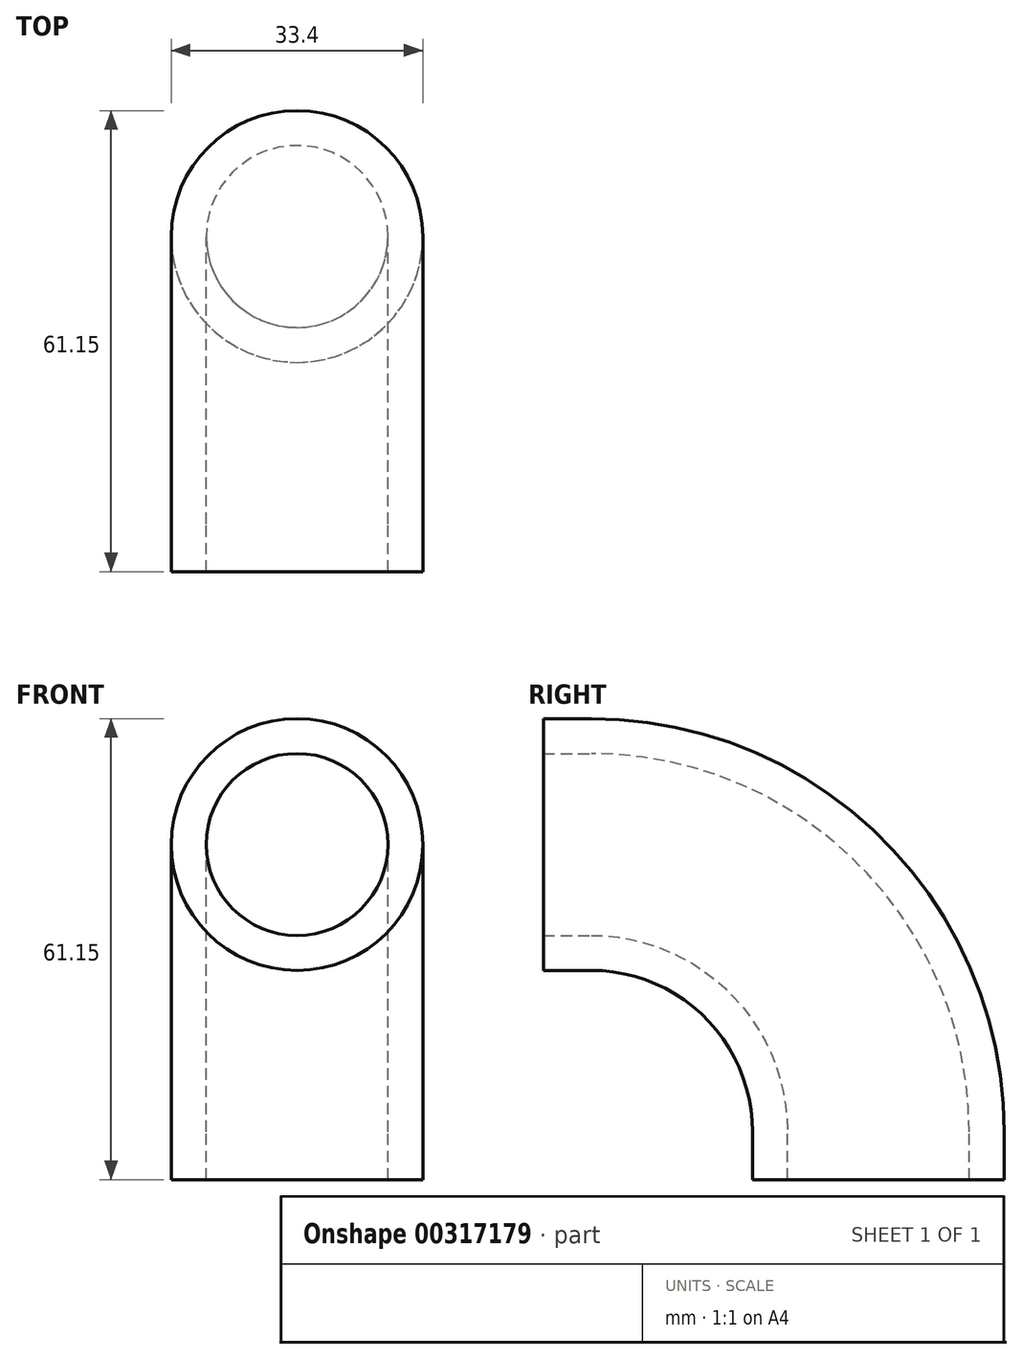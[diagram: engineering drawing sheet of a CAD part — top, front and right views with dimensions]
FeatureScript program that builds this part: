
annotation { "Feature Type Name" : "Feature", "Feature Type Description" : "" }
export const myFeature = defineFeature(function(context is Context, id is Id, definition is map)
    precondition{}
    {
        {
            var Q0;
            Q0=qCreatedBy(makeId("Right.planeOp"),FACE);
            var sketch = newSketch(context, id + "F0", { "sketchPlane" : qUnion([Q0])});
            skArc(sketch, "E0", {"start": v(38.1, 0) * mm, "mid": v(26.94, 26.94) * mm, "end": v(0, 38.1) * mm});
            skSolve(sketch);
        }
        {
            var Q0;
            Q0=qCreatedBy(makeId("Front.planeOp"),FACE);
            var sketch = newSketch(context, id + "F1", { "sketchPlane" : qUnion([Q0])});
            skCircle(sketch, "E1", {"center": v(0, 38.1) * mm, "radius": 16.7 * mm});
            skCircle(sketch, "E2", {"center": v(0, 38.1) * mm, "radius": 12.07 * mm});
            skSolve(sketch);
        }
        {
            var Q0;
            Q0=makeQuery(id+"F1.imprint","IMPRINT",FACE,{"disambiguationData":[TD([[makeQuery(id+"F1.imprint","IMPRINT",EDGE,{"derivedFrom":sQuery(id+"F1.wireOp",EDGE,"E1")}),1.0]])]});
            var Q1;
            Q1=sQuery(id+"F0.wireOp",EDGE,"E0");
            sweep(context, id + "F2", {"profiles" : qUnion([Q0]), "path" : qUnion([Q1])});
        }
        {
            var Q0;
            Q0=makeQuery(id+"F2.opSweep","CAP_FACE",FACE,{"disambiguationData":[OSD([sQuery(id+"F0.wireOp",VERTEX,"E0.end"),sQuery(id+"F1.wireOp",EDGE,"E1"),sQuery(id+"F1.wireOp",EDGE,"E2")])],"isStart":true});
            extrude(context, id + "F3", {"entities" : qUnion([Q0]), "operationType" : NewBodyOperationType.ADD, "depth" : 6.35 * mm});
        }
        {
            var Q0;
            Q0=makeQuery(id+"F2.opSweep","CAP_FACE",FACE,{"disambiguationData":[OSD([sQuery(id+"F0.wireOp",VERTEX,"E0.start"),sQuery(id+"F1.wireOp",EDGE,"E1"),sQuery(id+"F1.wireOp",EDGE,"E2")])],"isStart":false});
            extrude(context, id + "F4", {"entities" : qUnion([Q0]), "operationType" : NewBodyOperationType.ADD, "depth" : 6.35 * mm});
        }
    });
